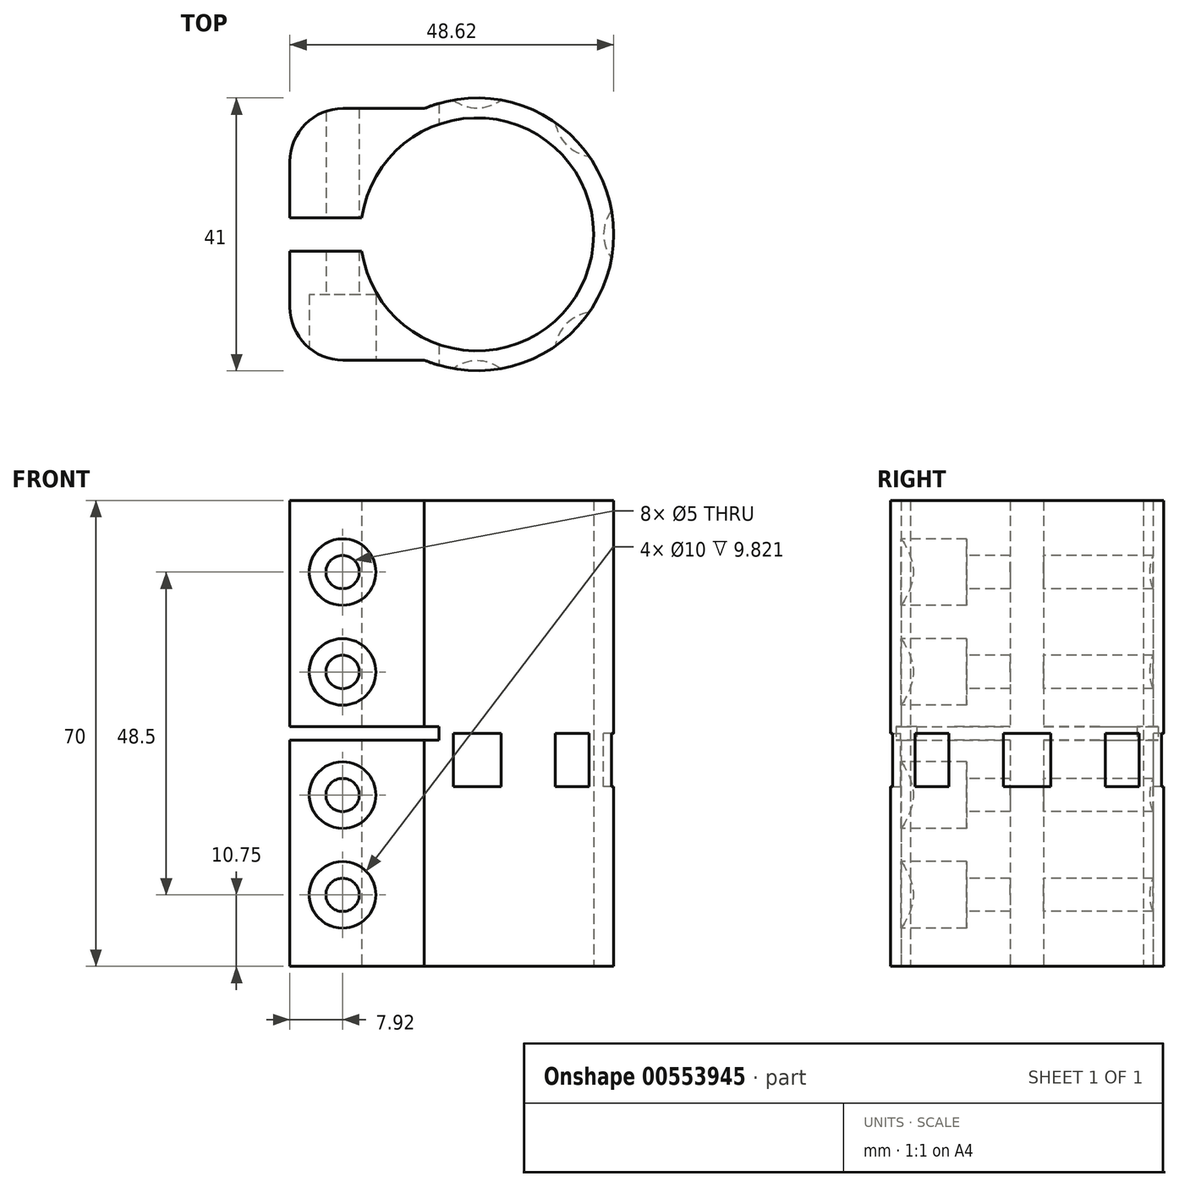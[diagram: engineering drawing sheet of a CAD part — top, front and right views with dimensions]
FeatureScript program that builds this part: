
annotation { "Feature Type Name" : "Feature", "Feature Type Description" : "" }
export const myFeature = defineFeature(function(context is Context, id is Id, definition is map)
    precondition{}
    {
        {
            var Q0;
            Q0=qCreatedBy(makeId("Top.planeOp"),FACE);
            var sketch = newSketch(context, id + "F0", { "sketchPlane" : qUnion([Q0])});
            skArc(sketch, "E0", {"start": v(-7.92, -18.9) * mm, "mid": v(20.5, 0) * mm, "end": v(-7.92, 18.9) * mm});
            skArc(sketch, "E1", {"start": v(-17.32, -2.5) * mm, "mid": v(17.5, 0) * mm, "end": v(-17.32, 2.5) * mm});
            skLineSegment(sketch, "E2", {"start": v(-7.92, 18.9) * mm, "end": v(-20.12, 18.9) * mm});
            skLineSegment(sketch, "E3", {"start": v(-28.12, 10.9) * mm, "end": v(-28.12, 2.5) * mm});
            skLineSegment(sketch, "E4", {"start": v(-28.12, 2.5) * mm, "end": v(-17.32, 2.5) * mm});
            skPoint(sketch, "E5.visualSharp", {"position": v(-28.12, 18.9) * mm});
            skArc(sketch, "E5.filletArc", {"start": v(-20.12, 18.9) * mm, "mid": v(-25.78, 16.57) * mm, "end": v(-28.12, 10.9) * mm});
            skLineSegment(sketch, "E6", {"start": v(0, 0) * mm, "end": v(29, 0) * mm, "construction": true});
            skLineSegment(sketch, "E7.MirrorCS", {"start": v(-28.12, -2.5) * mm, "end": v(-17.32, -2.5) * mm});
            skLineSegment(sketch, "E8.MirrorCS", {"start": v(-28.12, -10.9) * mm, "end": v(-28.12, -2.5) * mm});
            skArc(sketch, "E9.MirrorCS", {"start": v(-20.12, -18.9) * mm, "mid": v(-25.78, -16.57) * mm, "end": v(-28.12, -10.9) * mm});
            skLineSegment(sketch, "E10.MirrorCS", {"start": v(-7.92, -18.9) * mm, "end": v(-20.12, -18.9) * mm});
            skSolve(sketch);
        }
        {
            var Q0;
            Q0 = qSketchRegion(id + "F0", true);
            extrude(context, id + "F1", {"entities" : qUnion([Q0]), "endBound" : BoundingType.SYMMETRIC, "depth" : 70 * mm, "offsetDistance" : 25 * mm});
        }
        {
            var Q0;
            Q0=makeQuery(id+"F1.opExtrude","SWEPT_FACE",FACE,{"disambiguationData":[OSD([sQuery(id+"F0.wireOp",EDGE,"E10.MirrorCS")])]});
            var sketch = newSketch(context, id + "F2", { "sketchPlane" : qUnion([Q0])});
            skPoint(sketch, "E11", {"position": v(-20.2, -24.25) * mm});
            skPoint(sketch, "E12", {"position": v(-20.2, -9.25) * mm});
            skPoint(sketch, "E13", {"position": v(-20.2, 9.25) * mm});
            skPoint(sketch, "E14", {"position": v(-20.2, 24.25) * mm});
            skSolve(sketch);
        }
        {
            var Q0;
            Q0=sQuery(id+"F2.wireOp",VERTEX,"E11");
            var Q1;
            Q1=sQuery(id+"F2.wireOp",VERTEX,"E12");
            var Q2;
            Q2=sQuery(id+"F2.wireOp",VERTEX,"E13");
            var Q3;
            Q3=sQuery(id+"F2.wireOp",VERTEX,"E14");
            var Q4;
            Q4=makeQuery(id+"F1.opExtrude","SWEPT_BODY",BODY,{"disambiguationData":[OSD([sQuery(id+"F0.wireOp",EDGE,"E0"),sQuery(id+"F0.wireOp",EDGE,"E1"),sQuery(id+"F0.wireOp",EDGE,"E2"),sQuery(id+"F0.wireOp",EDGE,"E3"),sQuery(id+"F0.wireOp",EDGE,"E4"),sQuery(id+"F0.wireOp",EDGE,"E5.filletArc"),sQuery(id+"F0.wireOp",EDGE,"E7.MirrorCS"),sQuery(id+"F0.wireOp",EDGE,"E8.MirrorCS"),sQuery(id+"F0.wireOp",EDGE,"E9.MirrorCS"),sQuery(id+"F0.wireOp",EDGE,"E10.MirrorCS")])]});
            hole(context, id + "F3", {"style" : HoleStyle.C_BORE, "endStyle" : HoleEndStyle.THROUGH, "holeDiameter" : 5 * mm, "cBoreDiameter" : 10 * mm, "cBoreDepth" : 8 * mm, "majorDiameter" : 5 * mm, "isTappedThrough" : true, "tappedDepth" : 12 * mm, "tapClearance" : 3, "locations" : qUnion([Q0, Q1, Q2, Q3]), "scope" : qUnion([Q4])});
        }
        {
            var Q0;
            Q0=qCreatedBy(makeId("Front.planeOp"),FACE);
            var sketch = newSketch(context, id + "F4", { "sketchPlane" : qUnion([Q0])});
            skLineSegment(sketch, "E15.bottom", {"start": v(-28.12, 1) * mm, "end": v(-5.72, 1) * mm});
            skLineSegment(sketch, "E15.top", {"start": v(-28.12, -1) * mm, "end": v(-5.72, -1) * mm});
            skLineSegment(sketch, "E15.left", {"start": v(-28.12, 1) * mm, "end": v(-28.12, -1) * mm});
            skLineSegment(sketch, "E15.right", {"start": v(-5.72, 1) * mm, "end": v(-5.72, -1) * mm});
            skSolve(sketch);
        }
        {
            var Q0;
            Q0 = qSketchRegion(id + "F4", true);
            extrude(context, id + "F5", {"entities" : qUnion([Q0]), "operationType" : NewBodyOperationType.REMOVE, "endBound" : BoundingType.SYMMETRIC, "oppositeDirection" : true, "depth" : 50 * mm, "offsetDistance" : 25 * mm});
        }
        {
            var Q0;
            Q0=qCreatedBy(makeId("Top.planeOp"),FACE);
            var sketch = newSketch(context, id + "F6", { "sketchPlane" : qUnion([Q0])});
            skCircle(sketch, "E16", {"center": v(0, -25) * mm, "radius": 6 * mm});
            skCircle(sketch, "E17.1.0", {"center": v(17.68, -17.68) * mm, "radius": 6 * mm});
            skCircle(sketch, "E17.2.0", {"center": v(25, 0) * mm, "radius": 6 * mm});
            skCircle(sketch, "E17.3.0", {"center": v(17.68, 17.68) * mm, "radius": 6 * mm});
            skCircle(sketch, "E17.4.0", {"center": v(0, 25) * mm, "radius": 6 * mm});
            skPoint(sketch, "E17.center", {"position": v(0, 0) * mm});
            skLineSegment(sketch, "E17.anchor1", {"start": v(0, 0) * mm, "end": v(0, -25) * mm, "construction": true});
            skLineSegment(sketch, "E17.anchor2", {"start": v(0, 0) * mm, "end": v(0, 25) * mm, "construction": true});
            skSolve(sketch);
        }
        {
            var Q0;
            Q0 = qSketchRegion(id + "F6", true);
            extrude(context, id + "F7", {"entities" : qUnion([Q0]), "operationType" : NewBodyOperationType.REMOVE, "oppositeDirection" : true, "depth" : 8 * mm, "offsetDistance" : 25 * mm});
        }
    });
